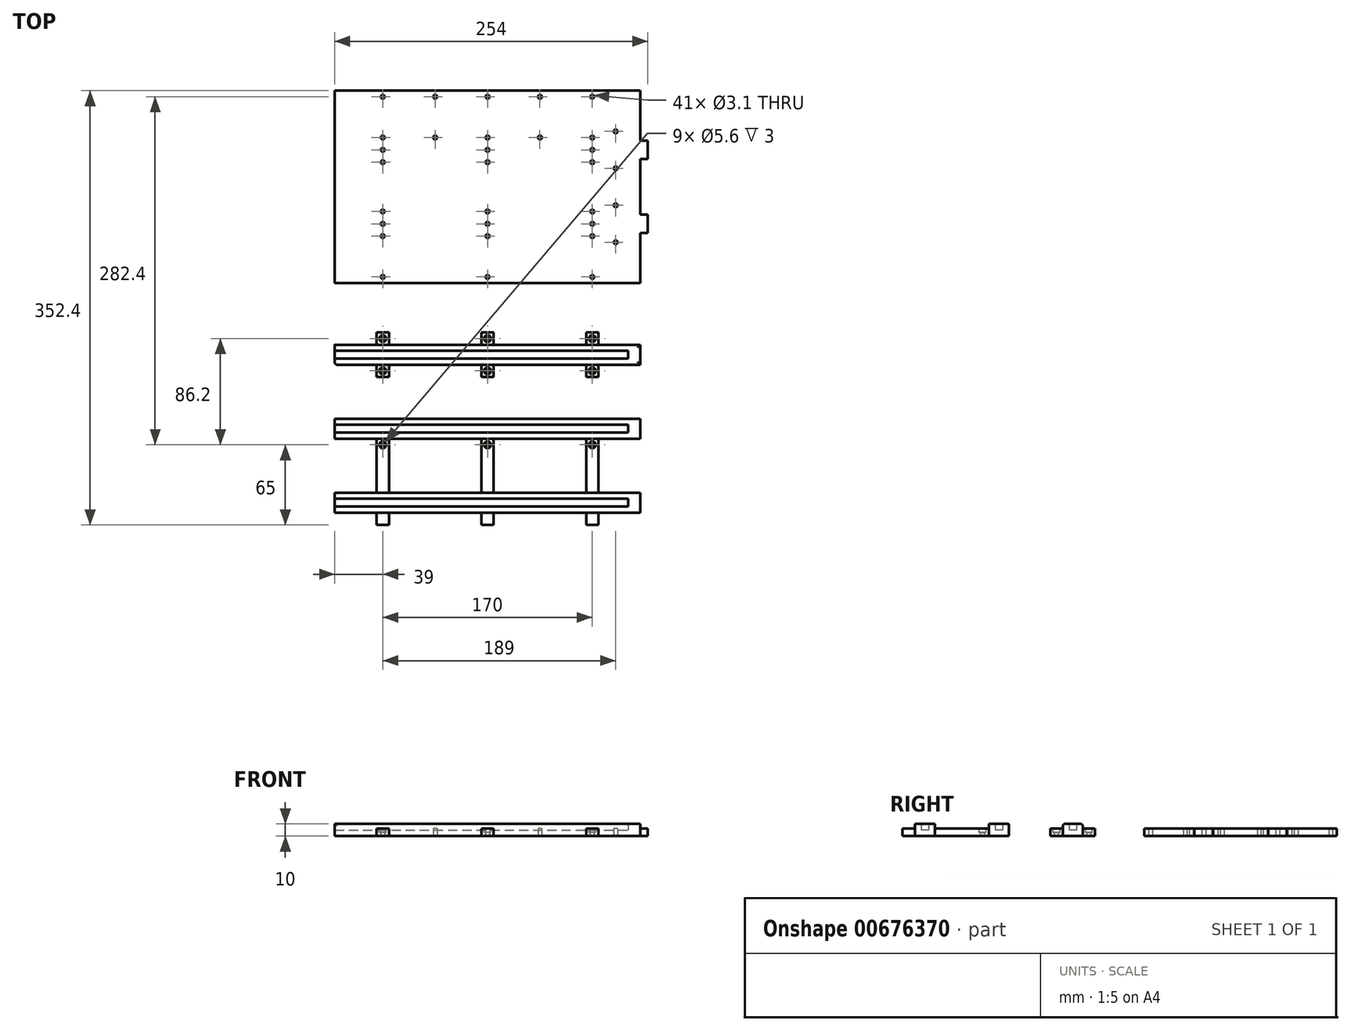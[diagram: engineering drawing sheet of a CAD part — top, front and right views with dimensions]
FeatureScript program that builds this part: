
annotation { "Feature Type Name" : "Feature", "Feature Type Description" : "" }
export const myFeature = defineFeature(function(context is Context, id is Id, definition is map)
    precondition{}
    {
        {
            var Q0;
            Q0=qCreatedBy(makeId("Top.planeOp"),FACE);
            var sketch = newSketch(context, id + "F0", { "sketchPlane" : qUnion([Q0])});
            skLineSegment(sketch, "E0.bottom", {"start": v(0, 0) * mm, "end": v(-248, 0) * mm});
            skLineSegment(sketch, "E0.top", {"start": v(0, 156.2) * mm, "end": v(-248, 156.2) * mm});
            skLineSegment(sketch, "E0.left", {"start": v(0, 0) * mm, "end": v(0, 156.2) * mm});
            skLineSegment(sketch, "E0.right", {"start": v(-248, 0) * mm, "end": v(-248, 156.2) * mm});
            skLineSegment(sketch, "E1", {"start": v(-124, 198.7) * mm, "end": v(-124, -29.13) * mm, "construction": true});
            skPoint(sketch, "E1.startSnap0", {"position": v(-124, 156.2) * mm});
            skLineSegment(sketch, "E2", {"start": v(0, 115.6) * mm, "end": v(6, 115.6) * mm});
            skLineSegment(sketch, "E3", {"start": v(6, 115.6) * mm, "end": v(6, 100.6) * mm});
            skLineSegment(sketch, "E4", {"start": v(6, 100.6) * mm, "end": v(0, 100.6) * mm});
            skLineSegment(sketch, "E5", {"start": v(0, 55.6) * mm, "end": v(6, 55.6) * mm});
            skLineSegment(sketch, "E6", {"start": v(6, 55.6) * mm, "end": v(6, 40.6) * mm});
            skLineSegment(sketch, "E7", {"start": v(6, 40.6) * mm, "end": v(0, 40.6) * mm});
            skPoint(sketch, "E8.centerSnap0", {"position": v(6, 108.1) * mm});
            skPoint(sketch, "E9.centerSnap0", {"position": v(6, 48.1) * mm});
            skLineSegment(sketch, "E10", {"start": v(0, -50) * mm, "end": v(-248, -50) * mm});
            skLineSegment(sketch, "E11", {"start": v(-248, -50) * mm, "end": v(-248, -66.2) * mm});
            skLineSegment(sketch, "E12", {"start": v(-248, -66.2) * mm, "end": v(0, -66.2) * mm});
            skLineSegment(sketch, "E13", {"start": v(0, -66.2) * mm, "end": v(0, -50) * mm});
            skLineSegment(sketch, "E14", {"start": v(0, -55) * mm, "end": v(-248, -55) * mm});
            skLineSegment(sketch, "E15", {"start": v(-248, -61.2) * mm, "end": v(0, -61.2) * mm});
            skLineSegment(sketch, "E16", {"start": v(-10, -55) * mm, "end": v(-10, -61.2) * mm});
            skLineSegment(sketch, "E17", {"start": v(0, -110) * mm, "end": v(-248, -110) * mm});
            skLineSegment(sketch, "E18", {"start": v(-248, -110) * mm, "end": v(-248, -126.2) * mm});
            skLineSegment(sketch, "E19", {"start": v(-248, -126.2) * mm, "end": v(0, -126.2) * mm});
            skLineSegment(sketch, "E20", {"start": v(0, -126.2) * mm, "end": v(0, -110) * mm});
            skLineSegment(sketch, "E21", {"start": v(0, -115) * mm, "end": v(-248, -115) * mm});
            skLineSegment(sketch, "E22", {"start": v(-248, -121.2) * mm, "end": v(0, -121.2) * mm});
            skLineSegment(sketch, "E23", {"start": v(-10, -115) * mm, "end": v(-10, -121.2) * mm});
            skLineSegment(sketch, "E24", {"start": v(0, -170) * mm, "end": v(-248, -170) * mm});
            skLineSegment(sketch, "E25", {"start": v(-248, -170) * mm, "end": v(-248, -186.2) * mm});
            skLineSegment(sketch, "E26", {"start": v(-248, -186.2) * mm, "end": v(0, -186.2) * mm});
            skLineSegment(sketch, "E27", {"start": v(0, -186.2) * mm, "end": v(0, -170) * mm});
            skLineSegment(sketch, "E28", {"start": v(0, -175) * mm, "end": v(-248, -175) * mm});
            skLineSegment(sketch, "E29", {"start": v(-248, -181.2) * mm, "end": v(0, -181.2) * mm});
            skLineSegment(sketch, "E30", {"start": v(-10, -175) * mm, "end": v(-10, -181.2) * mm});
            skLineSegment(sketch, "E31", {"start": v(-124, -66.2) * mm, "end": v(-124, -229.98) * mm, "construction": true});
            skPoint(sketch, "E31.endSnap0", {"position": v(-124, -186.2) * mm});
            skLineSegment(sketch, "E32", {"start": v(-119, -66.2) * mm, "end": v(-119, -110) * mm});
            skLineSegment(sketch, "E33", {"start": v(-119, -126.2) * mm, "end": v(-119, -170) * mm});
            skLineSegment(sketch, "E34.MirrorCS", {"start": v(-129, -66.2) * mm, "end": v(-129, -110) * mm});
            skLineSegment(sketch, "E35.MirrorCS", {"start": v(-129, -126.2) * mm, "end": v(-129, -170) * mm});
            skLineSegment(sketch, "E36", {"start": v(-204, -66.2) * mm, "end": v(-204, -110) * mm});
            skLineSegment(sketch, "E37", {"start": v(-214, -66.2) * mm, "end": v(-214, -110) * mm});
            skLineSegment(sketch, "E38", {"start": v(-204, -126.2) * mm, "end": v(-204, -170) * mm});
            skLineSegment(sketch, "E39", {"start": v(-214, -126.2) * mm, "end": v(-214, -170) * mm});
            skLineSegment(sketch, "E40.MirrorCS", {"start": v(-44, -66.2) * mm, "end": v(-44, -110) * mm});
            skLineSegment(sketch, "E41.MirrorCS", {"start": v(-34, -66.2) * mm, "end": v(-34, -110) * mm});
            skLineSegment(sketch, "E42.MirrorCS", {"start": v(-34, -126.2) * mm, "end": v(-34, -170) * mm});
            skLineSegment(sketch, "E43.MirrorCS", {"start": v(-44, -126.2) * mm, "end": v(-44, -170) * mm});
            skLineSegment(sketch, "E44", {"start": v(-204, -50) * mm, "end": v(-204, -40) * mm});
            skLineSegment(sketch, "E45", {"start": v(-204, -40) * mm, "end": v(-214, -40) * mm});
            skLineSegment(sketch, "E46", {"start": v(-214, -40) * mm, "end": v(-214, -50) * mm});
            skLineSegment(sketch, "E47.MirrorCS", {"start": v(-44, -50) * mm, "end": v(-44, -40) * mm});
            skLineSegment(sketch, "E48.MirrorCS", {"start": v(-44, -40) * mm, "end": v(-34, -40) * mm});
            skLineSegment(sketch, "E49.MirrorCS", {"start": v(-34, -40) * mm, "end": v(-34, -50) * mm});
            skLineSegment(sketch, "E50", {"start": v(-119, -50) * mm, "end": v(-119, -40) * mm});
            skLineSegment(sketch, "E51", {"start": v(-119, -40) * mm, "end": v(-129, -40) * mm});
            skLineSegment(sketch, "E52", {"start": v(-129, -40) * mm, "end": v(-129, -50) * mm});
            skLineSegment(sketch, "E53", {"start": v(-248, -118.1) * mm, "end": v(0, -118.1) * mm, "construction": true});
            skLineSegment(sketch, "E54.MirrorCS", {"start": v(-119, -186.2) * mm, "end": v(-119, -196.2) * mm});
            skLineSegment(sketch, "E55.MirrorCS", {"start": v(-129, -196.2) * mm, "end": v(-129, -186.2) * mm});
            skLineSegment(sketch, "E56.MirrorCS", {"start": v(-119, -196.2) * mm, "end": v(-129, -196.2) * mm});
            skLineSegment(sketch, "E57.MirrorCS", {"start": v(-44, -196.2) * mm, "end": v(-34, -196.2) * mm});
            skLineSegment(sketch, "E58.MirrorCS", {"start": v(-44, -186.2) * mm, "end": v(-44, -196.2) * mm});
            skLineSegment(sketch, "E59.MirrorCS", {"start": v(-34, -196.2) * mm, "end": v(-34, -186.2) * mm});
            skLineSegment(sketch, "E60.MirrorCS", {"start": v(-204, -186.2) * mm, "end": v(-204, -196.2) * mm});
            skLineSegment(sketch, "E61.MirrorCS", {"start": v(-204, -196.2) * mm, "end": v(-214, -196.2) * mm});
            skLineSegment(sketch, "E62.MirrorCS", {"start": v(-214, -196.2) * mm, "end": v(-214, -186.2) * mm});
            skCircle(sketch, "E63", {"center": v(-209, 5) * mm, "radius": 1.55 * mm});
            skCircle(sketch, "E64", {"center": v(-209, 38.1) * mm, "radius": 1.55 * mm});
            skCircle(sketch, "E65", {"center": v(-209, 48.1) * mm, "radius": 1.55 * mm});
            skCircle(sketch, "E66", {"center": v(-209, 58.1) * mm, "radius": 1.55 * mm});
            skCircle(sketch, "E67", {"center": v(-209, 118.1) * mm, "radius": 1.55 * mm});
            skCircle(sketch, "E68", {"center": v(-209, 108.1) * mm, "radius": 1.55 * mm});
            skCircle(sketch, "E69", {"center": v(-209, 98.1) * mm, "radius": 1.55 * mm});
            skCircle(sketch, "E70", {"center": v(-209, 151.2) * mm, "radius": 1.55 * mm});
            skLineSegment(sketch, "E71", {"start": v(-166.5, -24.63) * mm, "end": v(-166.5, 219.56) * mm, "construction": true});
            skCircle(sketch, "E72.MirrorC", {"center": v(-124, 58.1) * mm, "radius": 1.55 * mm});
            skCircle(sketch, "E73.MirrorC", {"center": v(-124, 5) * mm, "radius": 1.55 * mm});
            skCircle(sketch, "E74.MirrorC", {"center": v(-124, 38.1) * mm, "radius": 1.55 * mm});
            skCircle(sketch, "E75.MirrorC", {"center": v(-124, 48.1) * mm, "radius": 1.55 * mm});
            skCircle(sketch, "E76.MirrorC", {"center": v(-124, 98.1) * mm, "radius": 1.55 * mm});
            skCircle(sketch, "E77.MirrorC", {"center": v(-124, 151.2) * mm, "radius": 1.55 * mm});
            skCircle(sketch, "E78.MirrorC", {"center": v(-124, 118.1) * mm, "radius": 1.55 * mm});
            skCircle(sketch, "E79.MirrorC", {"center": v(-124, 108.1) * mm, "radius": 1.55 * mm});
            skCircle(sketch, "E80.MirrorC", {"center": v(-39, 151.2) * mm, "radius": 1.55 * mm});
            skCircle(sketch, "E81.MirrorC", {"center": v(-39, 118.1) * mm, "radius": 1.55 * mm});
            skCircle(sketch, "E82.MirrorC", {"center": v(-39, 108.1) * mm, "radius": 1.55 * mm});
            skCircle(sketch, "E83.MirrorC", {"center": v(-39, 98.1) * mm, "radius": 1.55 * mm});
            skCircle(sketch, "E84.MirrorC", {"center": v(-39, 38.1) * mm, "radius": 1.55 * mm});
            skCircle(sketch, "E85.MirrorC", {"center": v(-39, 48.1) * mm, "radius": 1.55 * mm});
            skCircle(sketch, "E86.MirrorC", {"center": v(-39, 58.1) * mm, "radius": 1.55 * mm});
            skCircle(sketch, "E87.MirrorC", {"center": v(-39, 5) * mm, "radius": 1.55 * mm});
            skCircle(sketch, "E88", {"center": v(-20, 123.1) * mm, "radius": 1.55 * mm});
            skCircle(sketch, "E89", {"center": v(-20, 93.1) * mm, "radius": 1.55 * mm});
            skCircle(sketch, "E90", {"center": v(-20, 63.1) * mm, "radius": 1.55 * mm});
            skCircle(sketch, "E91", {"center": v(-20, 33.1) * mm, "radius": 1.55 * mm});
            skCircle(sketch, "E92", {"center": v(-166.5, 151.2) * mm, "radius": 1.55 * mm});
            skCircle(sketch, "E93", {"center": v(-166.5, 118.1) * mm, "radius": 1.55 * mm});
            skCircle(sketch, "E94.MirrorC", {"center": v(-81.5, 151.2) * mm, "radius": 1.55 * mm});
            skCircle(sketch, "E95.MirrorC", {"center": v(-81.5, 118.1) * mm, "radius": 1.55 * mm});
            skLineSegment(sketch, "E96", {"start": v(-248, -286.2) * mm, "end": v(12, -286.2) * mm, "construction": true});
            skLineSegment(sketch, "E97.MirrorCS", {"start": v(-119, -376.2) * mm, "end": v(-129, -376.2) * mm});
            skLineSegment(sketch, "E98.MirrorCS", {"start": v(0, -446.2) * mm, "end": v(0, -462.4) * mm});
            skLineSegment(sketch, "E99.MirrorCS", {"start": v(-119, -532.4) * mm, "end": v(-129, -532.4) * mm});
            skLineSegment(sketch, "E100.MirrorCS", {"start": v(-204, -532.4) * mm, "end": v(-214, -532.4) * mm});
            skLineSegment(sketch, "E101.MirrorCS", {"start": v(-204, -376.2) * mm, "end": v(-214, -376.2) * mm});
            skLineSegment(sketch, "E102.MirrorCS", {"start": v(0, -386.2) * mm, "end": v(0, -402.4) * mm});
            skLineSegment(sketch, "E103.MirrorCS", {"start": v(-44, -532.4) * mm, "end": v(-34, -532.4) * mm});
            skLineSegment(sketch, "E104.MirrorCS", {"start": v(-44, -376.2) * mm, "end": v(-34, -376.2) * mm});
            skLineSegment(sketch, "E105.MirrorCS", {"start": v(-10, -457.4) * mm, "end": v(-10, -451.2) * mm});
            skLineSegment(sketch, "E106.MirrorCS", {"start": v(-129, -532.4) * mm, "end": v(-129, -522.4) * mm});
            skLineSegment(sketch, "E107.MirrorCS", {"start": v(-44, -522.4) * mm, "end": v(-44, -532.4) * mm});
            skLineSegment(sketch, "E108.MirrorCS", {"start": v(-204, -386.2) * mm, "end": v(-204, -376.2) * mm});
            skLineSegment(sketch, "E109.MirrorCS", {"start": v(-119, -522.4) * mm, "end": v(-119, -532.4) * mm});
            skLineSegment(sketch, "E110.MirrorCS", {"start": v(-248, -522.4) * mm, "end": v(-248, -506.2) * mm});
            skLineSegment(sketch, "E111.MirrorCS", {"start": v(-214, -532.4) * mm, "end": v(-214, -522.4) * mm});
            skLineSegment(sketch, "E112.MirrorCS", {"start": v(0, -506.2) * mm, "end": v(0, -522.4) * mm});
            skLineSegment(sketch, "E113.MirrorCS", {"start": v(-10, -397.4) * mm, "end": v(-10, -391.2) * mm});
            skLineSegment(sketch, "E114.MirrorCS", {"start": v(-214, -376.2) * mm, "end": v(-214, -386.2) * mm});
            skLineSegment(sketch, "E115.MirrorCS", {"start": v(-34, -532.4) * mm, "end": v(-34, -522.4) * mm});
            skLineSegment(sketch, "E116.MirrorCS", {"start": v(-34, -376.2) * mm, "end": v(-34, -386.2) * mm});
            skLineSegment(sketch, "E117.MirrorCS", {"start": v(-119, -386.2) * mm, "end": v(-119, -376.2) * mm});
            skLineSegment(sketch, "E118.MirrorCS", {"start": v(-248, -402.4) * mm, "end": v(-248, -386.2) * mm});
            skLineSegment(sketch, "E119.MirrorCS", {"start": v(-10, -517.4) * mm, "end": v(-10, -511.2) * mm});
            skLineSegment(sketch, "E120.MirrorCS", {"start": v(-248, -462.4) * mm, "end": v(-248, -446.2) * mm});
            skLineSegment(sketch, "E121.MirrorCS", {"start": v(-44, -386.2) * mm, "end": v(-44, -376.2) * mm});
            skLineSegment(sketch, "E122.MirrorCS", {"start": v(-129, -376.2) * mm, "end": v(-129, -386.2) * mm});
            skLineSegment(sketch, "E123.MirrorCS", {"start": v(-204, -522.4) * mm, "end": v(-204, -532.4) * mm});
            skLineSegment(sketch, "E124.MirrorCS", {"start": v(-248, -446.2) * mm, "end": v(0, -446.2) * mm});
            skLineSegment(sketch, "E125.MirrorCS", {"start": v(-119, -506.2) * mm, "end": v(-119, -462.4) * mm});
            skLineSegment(sketch, "E126.MirrorCS", {"start": v(-129, -506.2) * mm, "end": v(-129, -462.4) * mm});
            skLineSegment(sketch, "E127.MirrorCS", {"start": v(-204, -446.2) * mm, "end": v(-204, -402.4) * mm});
            skLineSegment(sketch, "E128.MirrorCS", {"start": v(0, -522.4) * mm, "end": v(-248, -522.4) * mm});
            skLineSegment(sketch, "E129.MirrorCS", {"start": v(0, -517.4) * mm, "end": v(-248, -517.4) * mm});
            skLineSegment(sketch, "E130.MirrorCS", {"start": v(0, -402.4) * mm, "end": v(-248, -402.4) * mm});
            skLineSegment(sketch, "E131.MirrorCS", {"start": v(-248, -511.2) * mm, "end": v(0, -511.2) * mm});
            skLineSegment(sketch, "E132.MirrorCS", {"start": v(-214, -506.2) * mm, "end": v(-214, -462.4) * mm});
            skLineSegment(sketch, "E133.MirrorCS", {"start": v(-248, -506.2) * mm, "end": v(0, -506.2) * mm});
            skLineSegment(sketch, "E134.MirrorCS", {"start": v(-248, -454.3) * mm, "end": v(0, -454.3) * mm, "construction": true});
            skLineSegment(sketch, "E135.MirrorCS", {"start": v(-119, -446.2) * mm, "end": v(-119, -402.4) * mm});
            skLineSegment(sketch, "E136.MirrorCS", {"start": v(0, -457.4) * mm, "end": v(-248, -457.4) * mm});
            skLineSegment(sketch, "E137.MirrorCS", {"start": v(-44, -446.2) * mm, "end": v(-44, -402.4) * mm});
            skLineSegment(sketch, "E138.MirrorCS", {"start": v(-248, -451.2) * mm, "end": v(0, -451.2) * mm});
            skLineSegment(sketch, "E139.MirrorCS", {"start": v(0, -397.4) * mm, "end": v(-248, -397.4) * mm});
            skLineSegment(sketch, "E140.MirrorCS", {"start": v(-34, -506.2) * mm, "end": v(-34, -462.4) * mm});
            skPoint(sketch, "E141.MirrorP", {"position": v(-124, -386.2) * mm});
            skLineSegment(sketch, "E142.MirrorCS", {"start": v(-214, -446.2) * mm, "end": v(-214, -402.4) * mm});
            skLineSegment(sketch, "E143.MirrorCS", {"start": v(-34, -446.2) * mm, "end": v(-34, -402.4) * mm});
            skLineSegment(sketch, "E144.MirrorCS", {"start": v(-248, -386.2) * mm, "end": v(0, -386.2) * mm});
            skLineSegment(sketch, "E145.MirrorCS", {"start": v(-44, -506.2) * mm, "end": v(-44, -462.4) * mm});
            skLineSegment(sketch, "E146.MirrorCS", {"start": v(0, -462.4) * mm, "end": v(-248, -462.4) * mm});
            skLineSegment(sketch, "E147.MirrorCS", {"start": v(-204, -506.2) * mm, "end": v(-204, -462.4) * mm});
            skLineSegment(sketch, "E148.MirrorCS", {"start": v(-129, -446.2) * mm, "end": v(-129, -402.4) * mm});
            skLineSegment(sketch, "E149.MirrorCS", {"start": v(-248, -391.2) * mm, "end": v(0, -391.2) * mm});
            skLineSegment(sketch, "E150", {"start": v(-214, -76.2) * mm, "end": v(-204, -76.2) * mm});
            skLineSegment(sketch, "E151", {"start": v(-129, -76.2) * mm, "end": v(-119, -76.2) * mm});
            skLineSegment(sketch, "E152", {"start": v(-44, -76.2) * mm, "end": v(-34, -76.2) * mm});
            skSolve(sketch);
        }
        {
            var Q0;
            {var subQ3=sQuery(id+"F0.wireOp",EDGE,"E0.bottom");Q0=makeQuery(id+"F0.imprint","IMPRINT",FACE,{"disambiguationData":[TD([[makeQuery(id+"F0.imprint","IMPRINT",EDGE,{"derivedFrom":subQ3}),-1.0]])]});}
            var Q1;
            {var subQ0=sQuery(id+"F0.wireOp",EDGE,"E2");Q1=makeQuery(id+"F0.imprint","IMPRINT",FACE,{"disambiguationData":[TD([[makeQuery(id+"F0.imprint","IMPRINT",EDGE,{"derivedFrom":subQ0}),-1.0]])]});}
            var Q2;
            {var subQ0=sQuery(id+"F0.wireOp",EDGE,"E5");Q2=makeQuery(id+"F0.imprint","IMPRINT",FACE,{"disambiguationData":[TD([[makeQuery(id+"F0.imprint","IMPRINT",EDGE,{"derivedFrom":subQ0}),-1.0]])]});}
            extrude(context, id + "F1", {"entities" : qUnion([Q0, Q1, Q2]), "depth" : 6 * mm, "offsetDistance" : 25 * mm});
        }
        {
            var Q0;
            {var subQ1=sQuery(id+"F0.wireOp",EDGE,"E12");var subQ9=sQuery(id+"F0.wireOp",EDGE,"E11");var subQ10=makeQuery(id+"F0.imprint","INTERSECT",VERTEX,{"derivedFrom":[subQ9,subQ1]});Q0=makeQuery(id+"F0.imprint","IMPRINT",FACE,{"disambiguationData":[TD([[makeQuery(id+"F0.imprint","IMPRINT",EDGE,{"disambiguationData":[TD([[subQ10,1.0]])],"derivedFrom":subQ9}),1.0]])]});}
            var Q1;
            {var subQ5=sQuery(id+"F0.wireOp",EDGE,"E16");Q1=makeQuery(id+"F0.imprint","IMPRINT",FACE,{"disambiguationData":[TD([[makeQuery(id+"F0.imprint","IMPRINT",EDGE,{"derivedFrom":subQ5}),-1.0]])]});}
            var Q2;
            {var subQ4=sQuery(id+"F0.wireOp",EDGE,"E10");Q2=makeQuery(id+"F0.imprint","IMPRINT",FACE,{"disambiguationData":[TD([[makeQuery(id+"F0.imprint","IMPRINT",EDGE,{"derivedFrom":subQ4}),1.0]])]});}
            var Q3;
            {var subQ5=sQuery(id+"F0.wireOp",EDGE,"E16");Q3=makeQuery(id+"F0.imprint","IMPRINT",FACE,{"disambiguationData":[TD([[makeQuery(id+"F0.imprint","IMPRINT",EDGE,{"derivedFrom":subQ5}),1.0]])]});}
            var Q4;
            {var subQ1=sQuery(id+"F0.wireOp",EDGE,"E20");var subQ4=sQuery(id+"F0.wireOp",EDGE,"E17");var subQ5=makeQuery(id+"F0.imprint","INTERSECT",VERTEX,{"derivedFrom":[subQ4,subQ1]});Q4=makeQuery(id+"F0.imprint","IMPRINT",FACE,{"disambiguationData":[TD([[makeQuery(id+"F0.imprint","IMPRINT",EDGE,{"disambiguationData":[TD([[subQ5,-1.0]])],"derivedFrom":subQ4}),1.0]])]});}
            var Q5;
            {var subQ5=sQuery(id+"F0.wireOp",EDGE,"E23");Q5=makeQuery(id+"F0.imprint","IMPRINT",FACE,{"disambiguationData":[TD([[makeQuery(id+"F0.imprint","IMPRINT",EDGE,{"derivedFrom":subQ5}),-1.0]])]});}
            var Q6;
            {var subQ1=sQuery(id+"F0.wireOp",EDGE,"E19");var subQ9=sQuery(id+"F0.wireOp",EDGE,"E18");var subQ10=makeQuery(id+"F0.imprint","INTERSECT",VERTEX,{"derivedFrom":[subQ9,subQ1]});Q6=makeQuery(id+"F0.imprint","IMPRINT",FACE,{"disambiguationData":[TD([[makeQuery(id+"F0.imprint","IMPRINT",EDGE,{"disambiguationData":[TD([[subQ10,1.0]])],"derivedFrom":subQ9}),1.0]])]});}
            var Q7;
            {var subQ5=sQuery(id+"F0.wireOp",EDGE,"E23");Q7=makeQuery(id+"F0.imprint","IMPRINT",FACE,{"disambiguationData":[TD([[makeQuery(id+"F0.imprint","IMPRINT",EDGE,{"derivedFrom":subQ5}),1.0]])]});}
            var Q8;
            {var subQ1=sQuery(id+"F0.wireOp",EDGE,"E24");var subQ8=sQuery(id+"F0.wireOp",EDGE,"E27");var subQ9=makeQuery(id+"F0.imprint","INTERSECT",VERTEX,{"derivedFrom":[subQ1,subQ8]});Q8=makeQuery(id+"F0.imprint","IMPRINT",FACE,{"disambiguationData":[TD([[makeQuery(id+"F0.imprint","IMPRINT",EDGE,{"disambiguationData":[TD([[subQ9,-1.0]])],"derivedFrom":subQ1}),1.0]])]});}
            var Q9;
            {var subQ5=sQuery(id+"F0.wireOp",EDGE,"E30");Q9=makeQuery(id+"F0.imprint","IMPRINT",FACE,{"disambiguationData":[TD([[makeQuery(id+"F0.imprint","IMPRINT",EDGE,{"derivedFrom":subQ5}),-1.0]])]});}
            var Q10;
            {var subQ5=sQuery(id+"F0.wireOp",EDGE,"E26");Q10=makeQuery(id+"F0.imprint","IMPRINT",FACE,{"disambiguationData":[TD([[makeQuery(id+"F0.imprint","IMPRINT",EDGE,{"derivedFrom":subQ5}),1.0]])]});}
            var Q11;
            {var subQ5=sQuery(id+"F0.wireOp",EDGE,"E30");Q11=makeQuery(id+"F0.imprint","IMPRINT",FACE,{"disambiguationData":[TD([[makeQuery(id+"F0.imprint","IMPRINT",EDGE,{"derivedFrom":subQ5}),1.0]])]});}
            extrude(context, id + "F2", {"entities" : qUnion([Q0, Q1, Q2, Q3, Q4, Q5, Q6, Q7, Q8, Q9, Q10, Q11]), "depth" : 5 * mm, "offsetDistance" : 25 * mm});
        }
        {
            var Q0;
            {var subQ5=sQuery(id+"F0.wireOp",EDGE,"E23");Q0=makeQuery(id+"F0.imprint","IMPRINT",FACE,{"disambiguationData":[TD([[makeQuery(id+"F0.imprint","IMPRINT",EDGE,{"derivedFrom":subQ5}),1.0]])]});}
            var Q1;
            {var subQ1=sQuery(id+"F0.wireOp",EDGE,"E20");var subQ4=sQuery(id+"F0.wireOp",EDGE,"E17");var subQ5=makeQuery(id+"F0.imprint","INTERSECT",VERTEX,{"derivedFrom":[subQ4,subQ1]});Q1=makeQuery(id+"F0.imprint","IMPRINT",FACE,{"disambiguationData":[TD([[makeQuery(id+"F0.imprint","IMPRINT",EDGE,{"disambiguationData":[TD([[subQ5,-1.0]])],"derivedFrom":subQ4}),1.0]])]});}
            var Q2;
            {var subQ1=sQuery(id+"F0.wireOp",EDGE,"E19");var subQ9=sQuery(id+"F0.wireOp",EDGE,"E18");var subQ10=makeQuery(id+"F0.imprint","INTERSECT",VERTEX,{"derivedFrom":[subQ9,subQ1]});Q2=makeQuery(id+"F0.imprint","IMPRINT",FACE,{"disambiguationData":[TD([[makeQuery(id+"F0.imprint","IMPRINT",EDGE,{"disambiguationData":[TD([[subQ10,1.0]])],"derivedFrom":subQ9}),1.0]])]});}
            var Q3;
            {var subQ1=sQuery(id+"F0.wireOp",EDGE,"E12");var subQ9=sQuery(id+"F0.wireOp",EDGE,"E11");var subQ10=makeQuery(id+"F0.imprint","INTERSECT",VERTEX,{"derivedFrom":[subQ9,subQ1]});Q3=makeQuery(id+"F0.imprint","IMPRINT",FACE,{"disambiguationData":[TD([[makeQuery(id+"F0.imprint","IMPRINT",EDGE,{"disambiguationData":[TD([[subQ10,1.0]])],"derivedFrom":subQ9}),1.0]])]});}
            var Q4;
            {var subQ4=sQuery(id+"F0.wireOp",EDGE,"E10");Q4=makeQuery(id+"F0.imprint","IMPRINT",FACE,{"disambiguationData":[TD([[makeQuery(id+"F0.imprint","IMPRINT",EDGE,{"derivedFrom":subQ4}),1.0]])]});}
            var Q5;
            {var subQ5=sQuery(id+"F0.wireOp",EDGE,"E16");Q5=makeQuery(id+"F0.imprint","IMPRINT",FACE,{"disambiguationData":[TD([[makeQuery(id+"F0.imprint","IMPRINT",EDGE,{"derivedFrom":subQ5}),1.0]])]});}
            var Q6;
            {var subQ1=sQuery(id+"F0.wireOp",EDGE,"E24");var subQ8=sQuery(id+"F0.wireOp",EDGE,"E27");var subQ9=makeQuery(id+"F0.imprint","INTERSECT",VERTEX,{"derivedFrom":[subQ1,subQ8]});Q6=makeQuery(id+"F0.imprint","IMPRINT",FACE,{"disambiguationData":[TD([[makeQuery(id+"F0.imprint","IMPRINT",EDGE,{"disambiguationData":[TD([[subQ9,-1.0]])],"derivedFrom":subQ1}),1.0]])]});}
            var Q7;
            {var subQ5=sQuery(id+"F0.wireOp",EDGE,"E30");Q7=makeQuery(id+"F0.imprint","IMPRINT",FACE,{"disambiguationData":[TD([[makeQuery(id+"F0.imprint","IMPRINT",EDGE,{"derivedFrom":subQ5}),1.0]])]});}
            var Q8;
            {var subQ5=sQuery(id+"F0.wireOp",EDGE,"E26");Q8=makeQuery(id+"F0.imprint","IMPRINT",FACE,{"disambiguationData":[TD([[makeQuery(id+"F0.imprint","IMPRINT",EDGE,{"derivedFrom":subQ5}),1.0]])]});}
            extrude(context, id + "F3", {"entities" : qUnion([Q0, Q1, Q2, Q3, Q4, Q5, Q6, Q7, Q8]), "operationType" : NewBodyOperationType.ADD, "depth" : 10 * mm, "offsetDistance" : 25 * mm});
        }
        {
            var Q0;
            {var subQ0=sQuery(id+"F0.wireOp",EDGE,"E42.MirrorCS");Q0=makeQuery(id+"F0.imprint","IMPRINT",FACE,{"disambiguationData":[TD([[makeQuery(id+"F0.imprint","IMPRINT",EDGE,{"derivedFrom":subQ0}),-1.0]])]});}
            var Q1;
            {var subQ0=sQuery(id+"F0.wireOp",EDGE,"E33");Q1=makeQuery(id+"F0.imprint","IMPRINT",FACE,{"disambiguationData":[TD([[makeQuery(id+"F0.imprint","IMPRINT",EDGE,{"derivedFrom":subQ0}),-1.0]])]});}
            var Q2;
            {var subQ0=sQuery(id+"F0.wireOp",EDGE,"E38");Q2=makeQuery(id+"F0.imprint","IMPRINT",FACE,{"disambiguationData":[TD([[makeQuery(id+"F0.imprint","IMPRINT",EDGE,{"derivedFrom":subQ0}),-1.0]])]});}
            var Q3;
            {var subQ0=sQuery(id+"F0.wireOp",EDGE,"E44");Q3=makeQuery(id+"F0.imprint","IMPRINT",FACE,{"disambiguationData":[TD([[makeQuery(id+"F0.imprint","IMPRINT",EDGE,{"derivedFrom":subQ0}),1.0]])]});}
            var Q4;
            {var subQ0=sQuery(id+"F0.wireOp",EDGE,"E50");Q4=makeQuery(id+"F0.imprint","IMPRINT",FACE,{"disambiguationData":[TD([[makeQuery(id+"F0.imprint","IMPRINT",EDGE,{"derivedFrom":subQ0}),1.0]])]});}
            var Q5;
            {var subQ0=sQuery(id+"F0.wireOp",EDGE,"E47.MirrorCS");Q5=makeQuery(id+"F0.imprint","IMPRINT",FACE,{"disambiguationData":[TD([[makeQuery(id+"F0.imprint","IMPRINT",EDGE,{"derivedFrom":subQ0}),-1.0]])]});}
            var Q6;
            {var subQ0=sQuery(id+"F0.wireOp",EDGE,"E60.MirrorCS");Q6=makeQuery(id+"F0.imprint","IMPRINT",FACE,{"disambiguationData":[TD([[makeQuery(id+"F0.imprint","IMPRINT",EDGE,{"derivedFrom":subQ0}),-1.0]])]});}
            var Q7;
            {var subQ0=sQuery(id+"F0.wireOp",EDGE,"E54.MirrorCS");Q7=makeQuery(id+"F0.imprint","IMPRINT",FACE,{"disambiguationData":[TD([[makeQuery(id+"F0.imprint","IMPRINT",EDGE,{"derivedFrom":subQ0}),-1.0]])]});}
            var Q8;
            Q8=makeQuery(id+"F0.imprint","IMPRINT",FACE,{"disambiguationData":[TD([[makeQuery(id+"F0.imprint","IMPRINT",EDGE,{"derivedFrom":sQuery(id+"F0.wireOp",EDGE,"E57.MirrorCS")}),1.0]])]});
            var Q9;
            {var subQ5=sQuery(id+"F0.wireOp",EDGE,"E152");Q9=makeQuery(id+"F0.imprint","IMPRINT",FACE,{"disambiguationData":[TD([[makeQuery(id+"F0.imprint","IMPRINT",EDGE,{"derivedFrom":subQ5}),1.0]])]});}
            var Q10;
            {var subQ5=sQuery(id+"F0.wireOp",EDGE,"E151");Q10=makeQuery(id+"F0.imprint","IMPRINT",FACE,{"disambiguationData":[TD([[makeQuery(id+"F0.imprint","IMPRINT",EDGE,{"derivedFrom":subQ5}),1.0]])]});}
            var Q11;
            {var subQ5=sQuery(id+"F0.wireOp",EDGE,"E150");Q11=makeQuery(id+"F0.imprint","IMPRINT",FACE,{"disambiguationData":[TD([[makeQuery(id+"F0.imprint","IMPRINT",EDGE,{"derivedFrom":subQ5}),1.0]])]});}
            extrude(context, id + "F4", {"entities" : qUnion([Q0, Q1, Q2, Q3, Q4, Q5, Q6, Q7, Q8, Q9, Q10, Q11]), "operationType" : NewBodyOperationType.ADD, "depth" : 6 * mm, "offsetDistance" : 25 * mm});
        }
        {
            var Q0;
            Q0=makeQuery(id+"F4.opExtrude","CAP_FACE",FACE,{"disambiguationData":[OSD([sQuery(id+"F0.wireOp",EDGE,"E12"),sQuery(id+"F0.wireOp",EDGE,"E17"),sQuery(id+"F0.wireOp",EDGE,"E36"),sQuery(id+"F0.wireOp",EDGE,"E37")])],"isStart":false});
            var sketch = newSketch(context, id + "F5", { "sketchPlane" : qUnion([Q0])});
            skCircle(sketch, "E153", {"center": v(-209, -71.2) * mm, "radius": 2.8 * mm});
            skCircle(sketch, "E154", {"center": v(-209, -71.2) * mm, "radius": 1.55 * mm});
            skCircle(sketch, "E155.0.1.0", {"center": v(-209, -131.2) * mm, "radius": 2.8 * mm});
            skCircle(sketch, "E155.0.1.1", {"center": v(-209, -131.2) * mm, "radius": 1.55 * mm});
            skCircle(sketch, "E155.1.0.0", {"center": v(-124, -71.2) * mm, "radius": 2.8 * mm});
            skCircle(sketch, "E155.1.0.1", {"center": v(-124, -71.2) * mm, "radius": 1.55 * mm});
            skCircle(sketch, "E155.1.1.0", {"center": v(-124, -131.2) * mm, "radius": 2.8 * mm});
            skCircle(sketch, "E155.1.1.1", {"center": v(-124, -131.2) * mm, "radius": 1.55 * mm});
            skCircle(sketch, "E155.2.0.0", {"center": v(-39, -71.2) * mm, "radius": 2.8 * mm});
            skCircle(sketch, "E155.2.0.1", {"center": v(-39, -71.2) * mm, "radius": 1.55 * mm});
            skCircle(sketch, "E155.2.1.0", {"center": v(-39, -131.2) * mm, "radius": 2.8 * mm});
            skCircle(sketch, "E155.2.1.1", {"center": v(-39, -131.2) * mm, "radius": 1.55 * mm});
            skLineSegment(sketch, "E155.direction1", {"start": v(-209, -71.2) * mm, "end": v(-124, -71.2) * mm, "construction": true});
            skLineSegment(sketch, "E155.direction2", {"start": v(-209, -71.2) * mm, "end": v(-209, -131.2) * mm, "construction": true});
            skCircle(sketch, "E156", {"center": v(-209, -45) * mm, "radius": 2.8 * mm});
            skCircle(sketch, "E157", {"center": v(-209, -45) * mm, "radius": 1.55 * mm});
            skCircle(sketch, "E158.1.0.0", {"center": v(-124, -45) * mm, "radius": 2.8 * mm});
            skCircle(sketch, "E158.1.0.1", {"center": v(-124, -45) * mm, "radius": 1.55 * mm});
            skCircle(sketch, "E158.2.0.0", {"center": v(-39, -45) * mm, "radius": 2.8 * mm});
            skCircle(sketch, "E158.2.0.1", {"center": v(-39, -45) * mm, "radius": 1.55 * mm});
            skLineSegment(sketch, "E158.direction1", {"start": v(-209, -45) * mm, "end": v(-124, -45) * mm, "construction": true});
            skSolve(sketch);
        }
        {
            var Q0;
            Q0=makeQuery(id+"F5.imprint","IMPRINT",FACE,{"disambiguationData":[TD([[makeQuery(id+"F5.imprint","IMPRINT",EDGE,{"derivedFrom":sQuery(id+"F5.wireOp",EDGE,"E154")}),1.0]])]});
            var Q1;
            Q1=makeQuery(id+"F5.imprint","IMPRINT",FACE,{"disambiguationData":[TD([[makeQuery(id+"F5.imprint","IMPRINT",EDGE,{"derivedFrom":sQuery(id+"F5.wireOp",EDGE,"KxXtiGmD-MxZM-oyGD-z7hu-39wdImJ7TbNY")}),1.0]])]});
            var Q2;
            Q2=makeQuery(id+"F5.imprint","IMPRINT",FACE,{"disambiguationData":[TD([[makeQuery(id+"F5.imprint","IMPRINT",EDGE,{"derivedFrom":sQuery(id+"F5.wireOp",EDGE,"j12ZK75k-Zkkb-ed7D-frRe-0mr0nYFnQjSL")}),1.0]])]});
            var Q3;
            Q3=makeQuery(id+"F5.imprint","IMPRINT",FACE,{"disambiguationData":[TD([[makeQuery(id+"F5.imprint","IMPRINT",EDGE,{"derivedFrom":sQuery(id+"F5.wireOp",EDGE,"E155.1.0.1")}),1.0]])]});
            var Q4;
            Q4=makeQuery(id+"F5.imprint","IMPRINT",FACE,{"disambiguationData":[TD([[makeQuery(id+"F5.imprint","IMPRINT",EDGE,{"derivedFrom":sQuery(id+"F5.wireOp",EDGE,"E155.1.0.3")}),1.0]])]});
            var Q5;
            Q5=makeQuery(id+"F5.imprint","IMPRINT",FACE,{"disambiguationData":[TD([[makeQuery(id+"F5.imprint","IMPRINT",EDGE,{"derivedFrom":sQuery(id+"F5.wireOp",EDGE,"E155.1.0.5")}),1.0]])]});
            var Q6;
            Q6=makeQuery(id+"F5.imprint","IMPRINT",FACE,{"disambiguationData":[TD([[makeQuery(id+"F5.imprint","IMPRINT",EDGE,{"derivedFrom":sQuery(id+"F5.wireOp",EDGE,"E155.2.0.1")}),1.0]])]});
            var Q7;
            Q7=makeQuery(id+"F5.imprint","IMPRINT",FACE,{"disambiguationData":[TD([[makeQuery(id+"F5.imprint","IMPRINT",EDGE,{"derivedFrom":sQuery(id+"F5.wireOp",EDGE,"E155.2.0.3")}),1.0]])]});
            var Q8;
            Q8=makeQuery(id+"F5.imprint","IMPRINT",FACE,{"disambiguationData":[TD([[makeQuery(id+"F5.imprint","IMPRINT",EDGE,{"derivedFrom":sQuery(id+"F5.wireOp",EDGE,"E155.2.0.5")}),1.0]])]});
            var Q9;
            Q9=makeQuery(id+"F5.imprint","IMPRINT",FACE,{"disambiguationData":[TD([[makeQuery(id+"F5.imprint","IMPRINT",EDGE,{"derivedFrom":sQuery(id+"F5.wireOp",EDGE,"E155.2.1.1")}),1.0]])]});
            var Q10;
            Q10=makeQuery(id+"F5.imprint","IMPRINT",FACE,{"disambiguationData":[TD([[makeQuery(id+"F5.imprint","IMPRINT",EDGE,{"derivedFrom":sQuery(id+"F5.wireOp",EDGE,"E155.2.1.3")}),1.0]])]});
            var Q11;
            Q11=makeQuery(id+"F5.imprint","IMPRINT",FACE,{"disambiguationData":[TD([[makeQuery(id+"F5.imprint","IMPRINT",EDGE,{"derivedFrom":sQuery(id+"F5.wireOp",EDGE,"E155.2.1.5")}),1.0]])]});
            var Q12;
            Q12=makeQuery(id+"F5.imprint","IMPRINT",FACE,{"disambiguationData":[TD([[makeQuery(id+"F5.imprint","IMPRINT",EDGE,{"derivedFrom":sQuery(id+"F5.wireOp",EDGE,"E155.1.1.1")}),1.0]])]});
            var Q13;
            Q13=makeQuery(id+"F5.imprint","IMPRINT",FACE,{"disambiguationData":[TD([[makeQuery(id+"F5.imprint","IMPRINT",EDGE,{"derivedFrom":sQuery(id+"F5.wireOp",EDGE,"E155.1.1.3")}),1.0]])]});
            var Q14;
            Q14=makeQuery(id+"F5.imprint","IMPRINT",FACE,{"disambiguationData":[TD([[makeQuery(id+"F5.imprint","IMPRINT",EDGE,{"derivedFrom":sQuery(id+"F5.wireOp",EDGE,"E155.1.1.5")}),1.0]])]});
            var Q15;
            Q15=makeQuery(id+"F5.imprint","IMPRINT",FACE,{"disambiguationData":[TD([[makeQuery(id+"F5.imprint","IMPRINT",EDGE,{"derivedFrom":sQuery(id+"F5.wireOp",EDGE,"E155.0.1.1")}),1.0]])]});
            var Q16;
            Q16=makeQuery(id+"F5.imprint","IMPRINT",FACE,{"disambiguationData":[TD([[makeQuery(id+"F5.imprint","IMPRINT",EDGE,{"derivedFrom":sQuery(id+"F5.wireOp",EDGE,"E155.0.1.3")}),1.0]])]});
            var Q17;
            Q17=makeQuery(id+"F5.imprint","IMPRINT",FACE,{"disambiguationData":[TD([[makeQuery(id+"F5.imprint","IMPRINT",EDGE,{"derivedFrom":sQuery(id+"F5.wireOp",EDGE,"E155.0.1.5")}),1.0]])]});
            var Q18;
            Q18=makeQuery(id+"F5.imprint","IMPRINT",FACE,{"disambiguationData":[TD([[makeQuery(id+"F5.imprint","IMPRINT",EDGE,{"derivedFrom":sQuery(id+"F5.wireOp",EDGE,"KDFxOcFq-m1sM-Pidf-AUfp-MyFMALyYsnj7")}),1.0]])]});
            var Q19;
            Q19=makeQuery(id+"F5.imprint","IMPRINT",FACE,{"disambiguationData":[TD([[makeQuery(id+"F5.imprint","IMPRINT",EDGE,{"derivedFrom":sQuery(id+"F5.wireOp",EDGE,"9ef58062-7159-40f5-b190-5eb6d7d90b25.1.0.0")}),1.0]])]});
            var Q20;
            Q20=makeQuery(id+"F5.imprint","IMPRINT",FACE,{"disambiguationData":[TD([[makeQuery(id+"F5.imprint","IMPRINT",EDGE,{"derivedFrom":sQuery(id+"F5.wireOp",EDGE,"9ef58062-7159-40f5-b190-5eb6d7d90b25.2.0.0")}),1.0]])]});
            var Q21;
            Q21=makeQuery(id+"F5.imprint","IMPRINT",FACE,{"disambiguationData":[TD([[makeQuery(id+"F5.imprint","IMPRINT",EDGE,{"derivedFrom":sQuery(id+"F5.wireOp",EDGE,"E157")}),1.0]])]});
            var Q22;
            Q22=makeQuery(id+"F5.imprint","IMPRINT",FACE,{"disambiguationData":[TD([[makeQuery(id+"F5.imprint","IMPRINT",EDGE,{"derivedFrom":sQuery(id+"F5.wireOp",EDGE,"E158.1.0.1")}),1.0]])]});
            var Q23;
            Q23=makeQuery(id+"F5.imprint","IMPRINT",FACE,{"disambiguationData":[TD([[makeQuery(id+"F5.imprint","IMPRINT",EDGE,{"derivedFrom":sQuery(id+"F5.wireOp",EDGE,"E158.2.0.1")}),1.0]])]});
            extrude(context, id + "F6", {"entities" : qUnion([Q0, Q1, Q2, Q3, Q4, Q5, Q6, Q7, Q8, Q9, Q10, Q11, Q12, Q13, Q14, Q15, Q16, Q17, Q18, Q19, Q20, Q21, Q22, Q23]), "operationType" : NewBodyOperationType.REMOVE, "oppositeDirection" : true, "depth" : 20 * mm, "offsetDistance" : 25 * mm, "hasSecondDirection" : true, "secondDirectionOppositeDirection" : false, "secondDirectionDepth" : 25 * mm});
        }
        {
            var Q0;
            Q0=makeQuery(id+"F5.imprint","IMPRINT",FACE,{"disambiguationData":[TD([[makeQuery(id+"F5.imprint","IMPRINT",EDGE,{"derivedFrom":sQuery(id+"F5.wireOp",EDGE,"cq5uAG0m-iSgZ-uiYW-Mkp8-4RP3VCPlkKiw")}),1.0]])]});
            var Q1;
            Q1=makeQuery(id+"F5.imprint","IMPRINT",FACE,{"disambiguationData":[TD([[makeQuery(id+"F5.imprint","IMPRINT",EDGE,{"derivedFrom":sQuery(id+"F5.wireOp",EDGE,"QUfd90mc-LF0u-Ryk3-H7xL-yYWbpMxUn6Ww")}),1.0]])]});
            var Q2;
            Q2=makeQuery(id+"F5.imprint","IMPRINT",FACE,{"disambiguationData":[TD([[makeQuery(id+"F5.imprint","IMPRINT",EDGE,{"derivedFrom":sQuery(id+"F5.wireOp",EDGE,"E153")}),1.0]])]});
            var Q3;
            Q3=makeQuery(id+"F5.imprint","IMPRINT",FACE,{"disambiguationData":[TD([[makeQuery(id+"F5.imprint","IMPRINT",EDGE,{"derivedFrom":sQuery(id+"F5.wireOp",EDGE,"E155.1.0.4")}),1.0]])]});
            var Q4;
            Q4=makeQuery(id+"F5.imprint","IMPRINT",FACE,{"disambiguationData":[TD([[makeQuery(id+"F5.imprint","IMPRINT",EDGE,{"derivedFrom":sQuery(id+"F5.wireOp",EDGE,"E155.1.0.2")}),1.0]])]});
            var Q5;
            Q5=makeQuery(id+"F5.imprint","IMPRINT",FACE,{"disambiguationData":[TD([[makeQuery(id+"F5.imprint","IMPRINT",EDGE,{"derivedFrom":sQuery(id+"F5.wireOp",EDGE,"E155.1.0.0")}),1.0]])]});
            var Q6;
            Q6=makeQuery(id+"F5.imprint","IMPRINT",FACE,{"disambiguationData":[TD([[makeQuery(id+"F5.imprint","IMPRINT",EDGE,{"derivedFrom":sQuery(id+"F5.wireOp",EDGE,"E155.2.0.4")}),1.0]])]});
            var Q7;
            Q7=makeQuery(id+"F5.imprint","IMPRINT",FACE,{"disambiguationData":[TD([[makeQuery(id+"F5.imprint","IMPRINT",EDGE,{"derivedFrom":sQuery(id+"F5.wireOp",EDGE,"E155.2.0.2")}),1.0]])]});
            var Q8;
            Q8=makeQuery(id+"F5.imprint","IMPRINT",FACE,{"disambiguationData":[TD([[makeQuery(id+"F5.imprint","IMPRINT",EDGE,{"derivedFrom":sQuery(id+"F5.wireOp",EDGE,"E155.2.0.0")}),1.0]])]});
            var Q9;
            Q9=makeQuery(id+"F5.imprint","IMPRINT",FACE,{"disambiguationData":[TD([[makeQuery(id+"F5.imprint","IMPRINT",EDGE,{"derivedFrom":sQuery(id+"F5.wireOp",EDGE,"E155.0.1.0")}),1.0]])]});
            var Q10;
            Q10=makeQuery(id+"F5.imprint","IMPRINT",FACE,{"disambiguationData":[TD([[makeQuery(id+"F5.imprint","IMPRINT",EDGE,{"derivedFrom":sQuery(id+"F5.wireOp",EDGE,"E155.0.1.2")}),1.0]])]});
            var Q11;
            Q11=makeQuery(id+"F5.imprint","IMPRINT",FACE,{"disambiguationData":[TD([[makeQuery(id+"F5.imprint","IMPRINT",EDGE,{"derivedFrom":sQuery(id+"F5.wireOp",EDGE,"E155.0.1.4")}),1.0]])]});
            var Q12;
            Q12=makeQuery(id+"F5.imprint","IMPRINT",FACE,{"disambiguationData":[TD([[makeQuery(id+"F5.imprint","IMPRINT",EDGE,{"derivedFrom":sQuery(id+"F5.wireOp",EDGE,"E155.1.1.4")}),1.0]])]});
            var Q13;
            Q13=makeQuery(id+"F5.imprint","IMPRINT",FACE,{"disambiguationData":[TD([[makeQuery(id+"F5.imprint","IMPRINT",EDGE,{"derivedFrom":sQuery(id+"F5.wireOp",EDGE,"E155.1.1.2")}),1.0]])]});
            var Q14;
            Q14=makeQuery(id+"F5.imprint","IMPRINT",FACE,{"disambiguationData":[TD([[makeQuery(id+"F5.imprint","IMPRINT",EDGE,{"derivedFrom":sQuery(id+"F5.wireOp",EDGE,"E155.1.1.0")}),1.0]])]});
            var Q15;
            Q15=makeQuery(id+"F5.imprint","IMPRINT",FACE,{"disambiguationData":[TD([[makeQuery(id+"F5.imprint","IMPRINT",EDGE,{"derivedFrom":sQuery(id+"F5.wireOp",EDGE,"E155.2.1.0")}),1.0]])]});
            var Q16;
            Q16=makeQuery(id+"F5.imprint","IMPRINT",FACE,{"disambiguationData":[TD([[makeQuery(id+"F5.imprint","IMPRINT",EDGE,{"derivedFrom":sQuery(id+"F5.wireOp",EDGE,"E155.2.1.2")}),1.0]])]});
            var Q17;
            Q17=makeQuery(id+"F5.imprint","IMPRINT",FACE,{"disambiguationData":[TD([[makeQuery(id+"F5.imprint","IMPRINT",EDGE,{"derivedFrom":sQuery(id+"F5.wireOp",EDGE,"E155.2.1.4")}),1.0]])]});
            var Q18;
            Q18=makeQuery(id+"F5.imprint","IMPRINT",FACE,{"disambiguationData":[TD([[makeQuery(id+"F5.imprint","IMPRINT",EDGE,{"derivedFrom":sQuery(id+"F5.wireOp",EDGE,"bIXkTzHi-Fame-2N83-VHJA-iyQKjjxmjPDN")}),1.0]])]});
            var Q19;
            Q19=makeQuery(id+"F5.imprint","IMPRINT",FACE,{"disambiguationData":[TD([[makeQuery(id+"F5.imprint","IMPRINT",EDGE,{"derivedFrom":sQuery(id+"F5.wireOp",EDGE,"9ef58062-7159-40f5-b190-5eb6d7d90b25.1.0.0")}),-1.0]])]});
            var Q20;
            Q20=makeQuery(id+"F5.imprint","IMPRINT",FACE,{"disambiguationData":[TD([[makeQuery(id+"F5.imprint","IMPRINT",EDGE,{"derivedFrom":sQuery(id+"F5.wireOp",EDGE,"9ef58062-7159-40f5-b190-5eb6d7d90b25.2.0.0")}),-1.0]])]});
            var Q21;
            Q21=makeQuery(id+"F5.imprint","IMPRINT",FACE,{"disambiguationData":[TD([[makeQuery(id+"F5.imprint","IMPRINT",EDGE,{"derivedFrom":sQuery(id+"F5.wireOp",EDGE,"E156")}),1.0]])]});
            var Q22;
            Q22=makeQuery(id+"F5.imprint","IMPRINT",FACE,{"disambiguationData":[TD([[makeQuery(id+"F5.imprint","IMPRINT",EDGE,{"derivedFrom":sQuery(id+"F5.wireOp",EDGE,"E158.1.0.0")}),1.0]])]});
            var Q23;
            Q23=makeQuery(id+"F5.imprint","IMPRINT",FACE,{"disambiguationData":[TD([[makeQuery(id+"F5.imprint","IMPRINT",EDGE,{"derivedFrom":sQuery(id+"F5.wireOp",EDGE,"E158.2.0.0")}),1.0]])]});
            extrude(context, id + "F7", {"entities" : qUnion([Q0, Q1, Q2, Q3, Q4, Q5, Q6, Q7, Q8, Q9, Q10, Q11, Q12, Q13, Q14, Q15, Q16, Q17, Q18, Q19, Q20, Q21, Q22, Q23]), "operationType" : NewBodyOperationType.REMOVE, "oppositeDirection" : true, "depth" : 3 * mm, "offsetDistance" : 25 * mm, "hasSecondDirection" : true, "secondDirectionOppositeDirection" : false, "secondDirectionDepth" : 25 * mm});
        }
        {
            var Q0;
            Q0=makeQuery(id+"F4.opExtrude","SWEPT_EDGE",EDGE,{"disambiguationData":[OSD([sQuery(id+"F0.wireOp",EDGE,"E12"),sQuery(id+"F0.wireOp",EDGE,"E37")])]});
            var Q1;
            Q1=makeQuery(id+"F4.opExtrude","SWEPT_EDGE",EDGE,{"disambiguationData":[OSD([sQuery(id+"F0.wireOp",EDGE,"E12"),sQuery(id+"F0.wireOp",EDGE,"E36")])]});
            var Q2;
            {var subQ0=sQuery(id+"F0.wireOp",EDGE,"E12");var subQ1=sQuery(id+"F0.wireOp",EDGE,"E11");Q2=makeQuery(id+"F3.boolean.opBoolean","MERGE",EDGE,{"derivedFrom":[makeQuery(id+"F2.opExtrude","SWEPT_EDGE",EDGE,{"disambiguationData":[OSD([subQ1,subQ0])]}),makeQuery(id+"F3.opExtrude","SWEPT_EDGE",EDGE,{"disambiguationData":[OSD([subQ1,subQ0])]})]});}
            var Q3;
            Q3=makeQuery(id+"F3.opExtrude","CAP_EDGE",EDGE,{"disambiguationData":[OSD([sQuery(id+"F0.wireOp",EDGE,"E12")])],"isStart":false});
            var Q4;
            Q4=makeQuery(id+"F4.opExtrude","SWEPT_EDGE",EDGE,{"disambiguationData":[OSD([sQuery(id+"F0.wireOp",EDGE,"E12"),sQuery(id+"F0.wireOp",EDGE,"E32")])]});
            var Q5;
            Q5=makeQuery(id+"F4.opExtrude","SWEPT_EDGE",EDGE,{"disambiguationData":[OSD([sQuery(id+"F0.wireOp",EDGE,"E12"),sQuery(id+"F0.wireOp",EDGE,"E34.MirrorCS")])]});
            var Q6;
            Q6=makeQuery(id+"F3.opExtrude","CAP_EDGE",EDGE,{"disambiguationData":[OSD([sQuery(id+"F0.wireOp",EDGE,"E13")])],"isStart":false});
            var Q7;
            Q7=makeQuery(id+"F3.opExtrude","CAP_EDGE",EDGE,{"disambiguationData":[OSD([sQuery(id+"F0.wireOp",EDGE,"E10")])],"isStart":false});
            var Q8;
            {var subQ0=sQuery(id+"F0.wireOp",EDGE,"E12");Q8=makeQuery(id+"F4.opExtrude","CAP_EDGE",EDGE,{"disambiguationData":[OSD([subQ0]),TDD([makeQuery(id+"F0.imprint","IMPRINT",EDGE,{"disambiguationData":[TD([[makeQuery(id+"F0.imprint","INTERSECT",VERTEX,{"derivedFrom":[subQ0,sQuery(id+"F0.wireOp",EDGE,"E40.MirrorCS")]}),-1.0]])],"derivedFrom":subQ0})])],"isStart":false});}
            var Q9;
            Q9=makeQuery(id+"F4.opExtrude","SWEPT_EDGE",EDGE,{"disambiguationData":[OSD([sQuery(id+"F0.wireOp",EDGE,"E12"),sQuery(id+"F0.wireOp",EDGE,"E40.MirrorCS")])]});
            var Q10;
            Q10=makeQuery(id+"F4.opExtrude","SWEPT_EDGE",EDGE,{"disambiguationData":[OSD([sQuery(id+"F0.wireOp",EDGE,"E12"),sQuery(id+"F0.wireOp",EDGE,"E41.MirrorCS")])]});
            var Q11;
            Q11=makeQuery(id+"F4.opExtrude","SWEPT_EDGE",EDGE,{"disambiguationData":[OSD([sQuery(id+"F0.wireOp",EDGE,"E10"),sQuery(id+"F0.wireOp",EDGE,"E49.MirrorCS")])]});
            var Q12;
            {var subQ0=sQuery(id+"F0.wireOp",EDGE,"E10");Q12=makeQuery(id+"F4.opExtrude","CAP_EDGE",EDGE,{"disambiguationData":[OSD([subQ0]),TDD([makeQuery(id+"F0.imprint","IMPRINT",EDGE,{"disambiguationData":[TD([[makeQuery(id+"F0.imprint","INTERSECT",VERTEX,{"derivedFrom":[subQ0,sQuery(id+"F0.wireOp",EDGE,"E47.MirrorCS")]}),1.0]])],"derivedFrom":subQ0})])],"isStart":false});}
            var Q13;
            Q13=makeQuery(id+"F4.opExtrude","SWEPT_EDGE",EDGE,{"disambiguationData":[OSD([sQuery(id+"F0.wireOp",EDGE,"E10"),sQuery(id+"F0.wireOp",EDGE,"E47.MirrorCS")])]});
            var Q14;
            {var subQ0=sQuery(id+"F0.wireOp",EDGE,"E12");Q14=makeQuery(id+"F4.opExtrude","CAP_EDGE",EDGE,{"disambiguationData":[OSD([subQ0]),TDD([makeQuery(id+"F0.imprint","IMPRINT",EDGE,{"disambiguationData":[TD([[makeQuery(id+"F0.imprint","INTERSECT",VERTEX,{"derivedFrom":[subQ0,sQuery(id+"F0.wireOp",EDGE,"E32")]}),1.0]])],"derivedFrom":subQ0})])],"isStart":false});}
            var Q15;
            {var subQ0=sQuery(id+"F0.wireOp",EDGE,"E12");Q15=makeQuery(id+"F4.opExtrude","CAP_EDGE",EDGE,{"disambiguationData":[OSD([subQ0]),TDD([makeQuery(id+"F0.imprint","IMPRINT",EDGE,{"disambiguationData":[TD([[makeQuery(id+"F0.imprint","INTERSECT",VERTEX,{"derivedFrom":[subQ0,sQuery(id+"F0.wireOp",EDGE,"E36")]}),1.0]])],"derivedFrom":subQ0})])],"isStart":false});}
            var Q16;
            {var subQ0=sQuery(id+"F0.wireOp",EDGE,"E10");Q16=makeQuery(id+"F4.opExtrude","CAP_EDGE",EDGE,{"disambiguationData":[OSD([subQ0]),TDD([makeQuery(id+"F0.imprint","IMPRINT",EDGE,{"disambiguationData":[TD([[makeQuery(id+"F0.imprint","INTERSECT",VERTEX,{"derivedFrom":[subQ0,sQuery(id+"F0.wireOp",EDGE,"E44")]}),-1.0]])],"derivedFrom":subQ0})])],"isStart":false});}
            var Q17;
            Q17=makeQuery(id+"F4.opExtrude","SWEPT_EDGE",EDGE,{"disambiguationData":[OSD([sQuery(id+"F0.wireOp",EDGE,"E10"),sQuery(id+"F0.wireOp",EDGE,"E44")])]});
            var Q18;
            Q18=makeQuery(id+"F4.opExtrude","SWEPT_EDGE",EDGE,{"disambiguationData":[OSD([sQuery(id+"F0.wireOp",EDGE,"E10"),sQuery(id+"F0.wireOp",EDGE,"E46")])]});
            var Q19;
            Q19=makeQuery(id+"F4.opExtrude","SWEPT_EDGE",EDGE,{"disambiguationData":[OSD([sQuery(id+"F0.wireOp",EDGE,"E10"),sQuery(id+"F0.wireOp",EDGE,"E52")])]});
            var Q20;
            {var subQ0=sQuery(id+"F0.wireOp",EDGE,"E10");Q20=makeQuery(id+"F4.opExtrude","CAP_EDGE",EDGE,{"disambiguationData":[OSD([subQ0]),TDD([makeQuery(id+"F0.imprint","IMPRINT",EDGE,{"disambiguationData":[TD([[makeQuery(id+"F0.imprint","INTERSECT",VERTEX,{"derivedFrom":[subQ0,sQuery(id+"F0.wireOp",EDGE,"E50")]}),-1.0]])],"derivedFrom":subQ0})])],"isStart":false});}
            var Q21;
            Q21=makeQuery(id+"F4.opExtrude","SWEPT_EDGE",EDGE,{"disambiguationData":[OSD([sQuery(id+"F0.wireOp",EDGE,"E10"),sQuery(id+"F0.wireOp",EDGE,"E50")])]});
            fillet(context, id + "F8", {"entities" : qUnion([Q0, Q1, Q2, Q3, Q4, Q5, Q6, Q7, Q8, Q9, Q10, Q11, Q12, Q13, Q14, Q15, Q16, Q17, Q18, Q19, Q20, Q21]), "tangentPropagation" : true, "radius" : 2 * mm, "defaultsChanged" : false, "vertexSettings" : [], "allowEdgeOverflow" : false});
        }
    });
